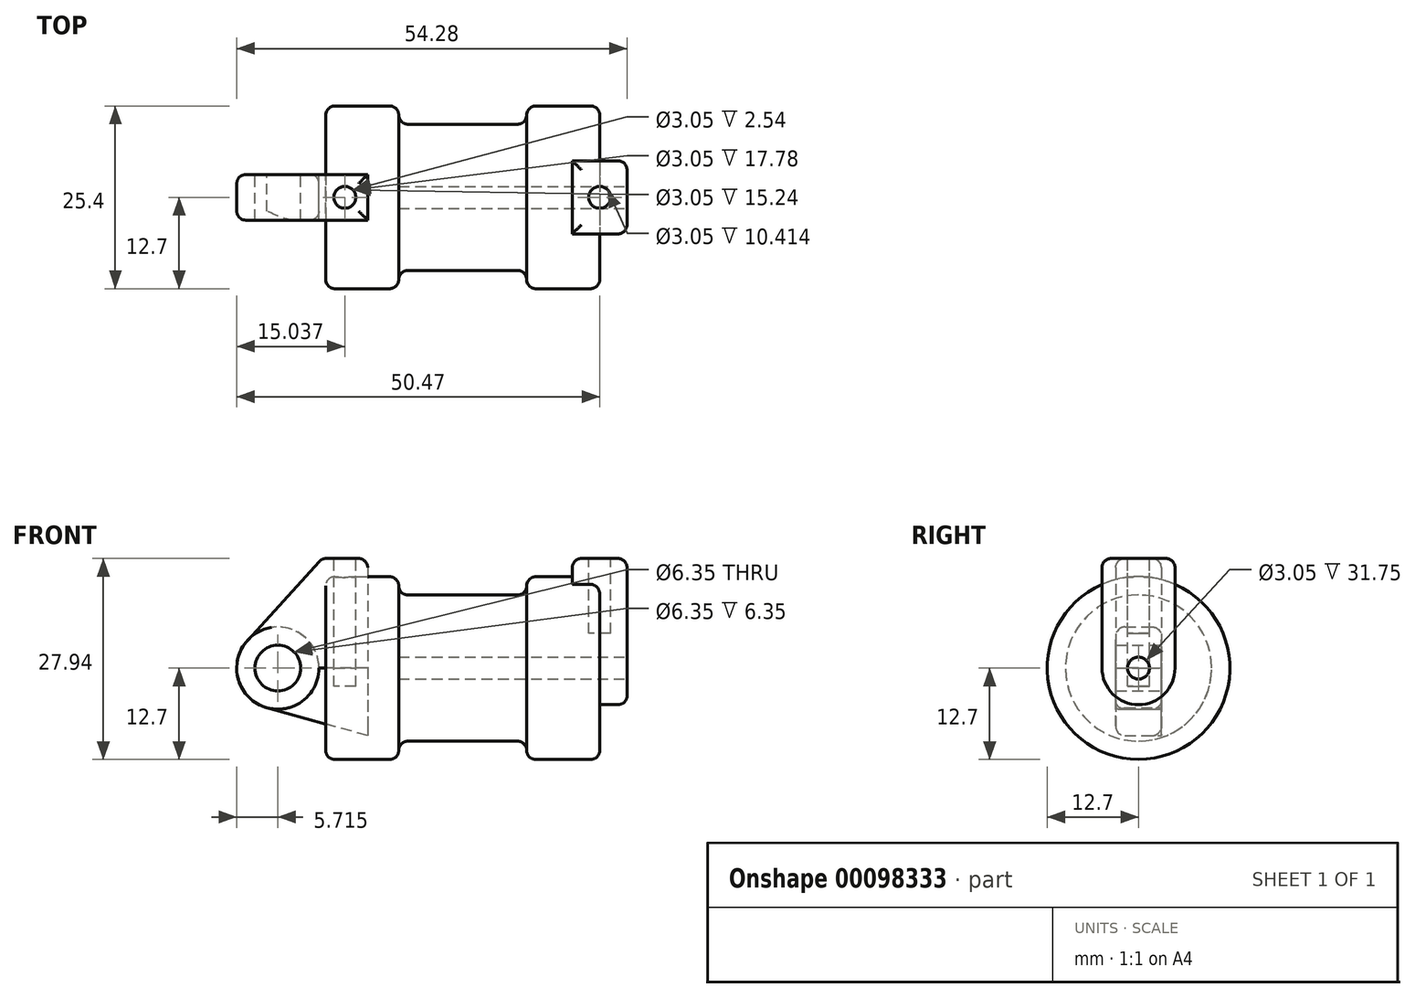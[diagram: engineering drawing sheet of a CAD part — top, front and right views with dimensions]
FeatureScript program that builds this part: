
annotation { "Feature Type Name" : "Feature", "Feature Type Description" : "" }
export const myFeature = defineFeature(function(context is Context, id is Id, definition is map)
    precondition{}
    {
        {
            var Q0;
            Q0=qCreatedBy(makeId("Front.planeOp"),FACE);
            var sketch = newSketch(context, id + "F0", { "sketchPlane" : qUnion([Q0])});
            skLineSegment(sketch, "E0", {"start": v(0, 0) * mm, "end": v(0, 12.7) * mm});
            skLineSegment(sketch, "E1", {"start": v(0, 12.7) * mm, "end": v(10.16, 12.7) * mm});
            skLineSegment(sketch, "E2", {"start": v(10.16, 12.7) * mm, "end": v(10.16, 10.16) * mm});
            skLineSegment(sketch, "E3", {"start": v(10.16, 10.16) * mm, "end": v(27.94, 10.16) * mm});
            skLineSegment(sketch, "E4", {"start": v(27.94, 10.16) * mm, "end": v(27.94, 12.7) * mm});
            skLineSegment(sketch, "E5", {"start": v(27.94, 12.7) * mm, "end": v(38.1, 12.7) * mm});
            skLineSegment(sketch, "E6", {"start": v(38.1, 12.7) * mm, "end": v(38.1, 0) * mm});
            skLineSegment(sketch, "E7", {"start": v(38.1, 0) * mm, "end": v(0, 0) * mm});
            skLineSegment(sketch, "E8", {"start": v(5.84, 15.24) * mm, "end": v(-0.5, 15.24) * mm});
            skLineSegment(sketch, "E9", {"start": v(-0.5, 15.24) * mm, "end": v(-10.88, 3.85) * mm});
            skLineSegment(sketch, "E10", {"start": v(0, 0) * mm, "end": v(-6.65, 0) * mm});
            skCircle(sketch, "E11", {"center": v(-6.65, 0) * mm, "radius": 5.72 * mm});
            skCircle(sketch, "E12", {"center": v(-6.65, 0) * mm, "radius": 3.18 * mm});
            skLineSegment(sketch, "E13", {"start": v(5.84, 15.24) * mm, "end": v(5.84, -9.4) * mm});
            skLineSegment(sketch, "E14", {"start": v(5.84, -9.4) * mm, "end": v(-8.18, -5.5) * mm});
            skSolve(sketch);
        }
        {
            var Q0;
            {var subQ0=sQuery(id+"F0.wireOp",EDGE,"E2");Q0=makeQuery(id+"F0.imprint","IMPRINT",FACE,{"disambiguationData":[TD([[makeQuery(id+"F0.imprint","IMPRINT",EDGE,{"derivedFrom":subQ0}),-1.0]])]});}
            var Q1;
            {var subQ0=sQuery(id+"F0.wireOp",EDGE,"E0");Q1=makeQuery(id+"F0.imprint","IMPRINT",FACE,{"disambiguationData":[TD([[makeQuery(id+"F0.imprint","IMPRINT",EDGE,{"derivedFrom":subQ0}),-1.0]])]});}
            var Q2;
            Q2=sQuery(id+"F0.wireOp",EDGE,"E7");
            revolve(context, id + "F1", {"entities" : qUnion([Q0, Q1]), "axis" : qUnion([Q2]), "revolveType" : RevolveType.FULL});
        }
        {
            var Q0;
            {var subQ4=sQuery(id+"F0.wireOp",EDGE,"E12");Q0=makeQuery(id+"F0.imprint","IMPRINT",FACE,{"disambiguationData":[TD([[makeQuery(id+"F0.imprint","IMPRINT",EDGE,{"derivedFrom":subQ4}),-1.0]])]});}
            extrude(context, id + "F2", {"entities" : qUnion([Q0]), "operationType" : NewBodyOperationType.ADD, "endBound" : BoundingType.SYMMETRIC, "depth" : 6.35 * mm});
        }
        {
            var Q0;
            {var subQ3=sQuery(id+"F0.wireOp",EDGE,"E0");Q0=makeQuery(id+"F0.imprint","IMPRINT",FACE,{"disambiguationData":[TD([[makeQuery(id+"F0.imprint","IMPRINT",EDGE,{"derivedFrom":subQ3}),1.0]])]});}
            var Q1;
            {var subQ0=sQuery(id+"F0.wireOp",EDGE,"E14");Q1=makeQuery(id+"F0.imprint","IMPRINT",FACE,{"disambiguationData":[TD([[makeQuery(id+"F0.imprint","IMPRINT",EDGE,{"derivedFrom":subQ0}),-1.0]])]});}
            var Q2;
            {var subQ4=sQuery(id+"F0.wireOp",EDGE,"E12");Q2=makeQuery(id+"F0.imprint","IMPRINT",FACE,{"disambiguationData":[TD([[makeQuery(id+"F0.imprint","IMPRINT",EDGE,{"derivedFrom":subQ4}),-1.0]])]});}
            var Q3;
            {var subQ0=sQuery(id+"F0.wireOp",EDGE,"E0");Q3=makeQuery(id+"F0.imprint","IMPRINT",FACE,{"disambiguationData":[TD([[makeQuery(id+"F0.imprint","IMPRINT",EDGE,{"derivedFrom":subQ0}),-1.0]])]});}
            extrude(context, id + "F3", {"entities" : qUnion([Q0, Q1, Q2, Q3]), "endBound" : BoundingType.SYMMETRIC, "depth" : 6.35 * mm});
        }
        {
            var Q0;
            {var subQ0=sQuery(id+"F0.wireOp",EDGE,"E14");Q0=makeQuery(id+"F0.imprint","IMPRINT",FACE,{"disambiguationData":[TD([[makeQuery(id+"F0.imprint","IMPRINT",EDGE,{"derivedFrom":subQ0}),-1.0]])]});}
            extrude(context, id + "F4", {"entities" : qUnion([Q0]), "endBound" : BoundingType.SYMMETRIC, "depth" : 6.35 * mm});
        }
        {
            var Q0;
            Q0=makeQuery(id+"F1.opRevolve","SWEPT_FACE",FACE,{"disambiguationData":[OSD([sQuery(id+"F0.wireOp",EDGE,"E6")])]});
            var sketch = newSketch(context, id + "F5", { "sketchPlane" : qUnion([Q0])});
            skCircle(sketch, "E15", {"center": v(0, 0) * mm, "radius": 1.52 * mm});
            skCircle(sketch, "E16", {"center": v(0, 0) * mm, "radius": 5.08 * mm});
            skLineSegment(sketch, "E17", {"start": v(-5.08, 0) * mm, "end": v(-5.08, 15.24) * mm});
            skLineSegment(sketch, "E18", {"start": v(5.08, 0) * mm, "end": v(5.08, 15.24) * mm});
            skLineSegment(sketch, "E19", {"start": v(-5.08, 15.24) * mm, "end": v(5.08, 15.24) * mm});
            skSolve(sketch);
        }
        {
            var Q0;
            {var subQ0=sQuery(id+"F5.wireOp",EDGE,"E19");Q0=makeQuery(id+"F5.imprint","IMPRINT",FACE,{"disambiguationData":[TD([[makeQuery(id+"F5.imprint","IMPRINT",EDGE,{"derivedFrom":subQ0}),-1.0]])]});}
            var Q1;
            {var subQ0=sQuery(id+"F5.wireOp",EDGE,"E17");var subQ1=sQuery(id+"F5.wireOp",EDGE,"E16");var subQ2=makeQuery(id+"F5.imprint","INTERSECT",VERTEX,{"derivedFrom":[subQ1,subQ0]});Q1=makeQuery(id+"F5.imprint","IMPRINT",FACE,{"disambiguationData":[TD([[makeQuery(id+"F5.imprint","IMPRINT",EDGE,{"disambiguationData":[TD([[subQ2,1.0]])],"derivedFrom":subQ1}),-1.0]])]});}
            var Q2;
            Q2=makeQuery(id+"F5.imprint","IMPRINT",FACE,{"disambiguationData":[TD([[makeQuery(id+"F5.imprint","IMPRINT",EDGE,{"derivedFrom":sQuery(id+"F5.wireOp",EDGE,"E15")}),-1.0]])]});
            extrude(context, id + "F6", {"entities" : qUnion([Q0, Q1, Q2]), "operationType" : NewBodyOperationType.ADD, "endBound" : BoundingType.SYMMETRIC, "oppositeDirection" : true, "depth" : 7.62 * mm});
        }
        {
            var Q0;
            Q0=makeQuery(id+"F5.imprint","IMPRINT",FACE,{"disambiguationData":[TD([[makeQuery(id+"F5.imprint","IMPRINT",EDGE,{"derivedFrom":sQuery(id+"F5.wireOp",EDGE,"E15")}),1.0]])]});
            var Q1;
            Q1=makeQuery(id+"F1.opRevolve","SWEPT_FACE",FACE,{"disambiguationData":[OSD([sQuery(id+"F0.wireOp",EDGE,"E2")])]});
            extrude(context, id + "F7", {"entities" : qUnion([Q0]), "operationType" : NewBodyOperationType.REMOVE, "endBound" : BoundingType.UP_TO_SURFACE, "oppositeDirection" : true, "endBoundEntityFace" : qUnion([Q1]), "depth" : 25.4 * mm});
        }
        {
            var Q0;
            Q0=makeQuery(id+"F3.opExtrude","SWEPT_FACE",FACE,{"disambiguationData":[OSD([sQuery(id+"F0.wireOp",EDGE,"E8")])]});
            var sketch = newSketch(context, id + "F8", { "sketchPlane" : qUnion([Q0])});
            skCircle(sketch, "E20", {"center": v(38.1, 0) * mm, "radius": 1.52 * mm});
            skPoint(sketch, "E21", {"position": v(2.67, 0) * mm});
            skCircle(sketch, "E22", {"center": v(2.67, 0) * mm, "radius": 1.52 * mm});
            skSolve(sketch);
        }
        {
            var Q0;
            Q0=makeQuery(id+"F8.imprint","IMPRINT",FACE,{"disambiguationData":[TD([[makeQuery(id+"F8.imprint","IMPRINT",EDGE,{"derivedFrom":sQuery(id+"F8.wireOp",EDGE,"E22")}),1.0]])]});
            var Q1;
            Q1=sQuery(id+"F8.wireOp",EDGE,"E22");
            extrude(context, id + "F9", {"entities" : qUnion([Q0]), "operationType" : NewBodyOperationType.REMOVE, "surfaceEntities" : qUnion([Q1]), "oppositeDirection" : true, "depth" : 17.78 * mm});
        }
        {
            var Q0;
            Q0=makeQuery(id+"F8.imprint","IMPRINT",FACE,{"disambiguationData":[TD([[makeQuery(id+"F8.imprint","IMPRINT",EDGE,{"derivedFrom":sQuery(id+"F8.wireOp",EDGE,"E20")}),1.0]])]});
            var Q1;
            Q1=sQuery(id+"F8.wireOp",EDGE,"E20");
            extrude(context, id + "F10", {"entities" : qUnion([Q0]), "operationType" : NewBodyOperationType.REMOVE, "surfaceEntities" : qUnion([Q1]), "oppositeDirection" : true, "depth" : 10.4 * mm});
        }
        {
            var Q0;
            Q0=makeQuery(id+"F1.opRevolve","SWEPT_EDGE",EDGE,{"disambiguationData":[OSD([sQuery(id+"F0.wireOp",EDGE,"E2"),sQuery(id+"F0.wireOp",EDGE,"E3")])]});
            var Q1;
            Q1=makeQuery(id+"F1.opRevolve","SWEPT_EDGE",EDGE,{"disambiguationData":[OSD([sQuery(id+"F0.wireOp",EDGE,"E1"),sQuery(id+"F0.wireOp",EDGE,"E2")])]});
            var Q2;
            Q2=makeQuery(id+"F1.opRevolve","SWEPT_EDGE",EDGE,{"disambiguationData":[OSD([sQuery(id+"F0.wireOp",EDGE,"E4"),sQuery(id+"F0.wireOp",EDGE,"E5")])]});
            var Q3;
            Q3=makeQuery(id+"F1.opRevolve","SWEPT_EDGE",EDGE,{"disambiguationData":[OSD([sQuery(id+"F0.wireOp",EDGE,"E3"),sQuery(id+"F0.wireOp",EDGE,"E4")])]});
            var Q4;
            Q4=makeQuery(id+"F1.opRevolve","SWEPT_EDGE",EDGE,{"disambiguationData":[OSD([sQuery(id+"F0.wireOp",EDGE,"E5"),sQuery(id+"F0.wireOp",EDGE,"E6")])]});
            var Q5;
            Q5=makeQuery(id+"F6.opExtrude","CAP_EDGE",EDGE,{"disambiguationData":[OSD([sQuery(id+"F5.wireOp",EDGE,"E19")])],"isStart":true});
            var Q6;
            Q6=makeQuery(id+"F6.opExtrude","SWEPT_EDGE",EDGE,{"disambiguationData":[OSD([sQuery(id+"F5.wireOp",EDGE,"E18"),sQuery(id+"F5.wireOp",EDGE,"E19")])]});
            var Q7;
            Q7=makeQuery(id+"F6.opExtrude","CAP_EDGE",EDGE,{"disambiguationData":[OSD([sQuery(id+"F5.wireOp",EDGE,"E19")])],"isStart":false});
            var Q8;
            Q8=makeQuery(id+"F6.opExtrude","SWEPT_EDGE",EDGE,{"disambiguationData":[OSD([sQuery(id+"F5.wireOp",EDGE,"E17"),sQuery(id+"F5.wireOp",EDGE,"E19")])]});
            var Q9;
            Q9=makeQuery(id+"F6.opExtrude","CAP_EDGE",EDGE,{"disambiguationData":[OSD([sQuery(id+"F5.wireOp",EDGE,"E16")])],"isStart":true});
            var Q10;
            Q10=makeQuery(id+"F6.opExtrude","CAP_EDGE",EDGE,{"disambiguationData":[OSD([sQuery(id+"F5.wireOp",EDGE,"E17")])],"isStart":true});
            var Q11;
            Q11=makeQuery(id+"F3.opExtrude","CAP_EDGE",EDGE,{"disambiguationData":[OSD([sQuery(id+"F0.wireOp",EDGE,"E8")])],"isStart":true});
            var Q12;
            Q12=makeQuery(id+"F3.opExtrude","SWEPT_EDGE",EDGE,{"disambiguationData":[OSD([sQuery(id+"F0.wireOp",EDGE,"E8"),sQuery(id+"F0.wireOp",EDGE,"E13")])]});
            var Q13;
            Q13=makeQuery(id+"F3.opExtrude","CAP_EDGE",EDGE,{"disambiguationData":[OSD([sQuery(id+"F0.wireOp",EDGE,"E8")])],"isStart":false});
            var Q14;
            Q14=makeQuery(id+"F3.opExtrude","SWEPT_EDGE",EDGE,{"disambiguationData":[OSD([sQuery(id+"F0.wireOp",EDGE,"E8"),sQuery(id+"F0.wireOp",EDGE,"E9")])]});
            var Q15;
            Q15=makeQuery(id+"F4.opExtrude","CAP_EDGE",EDGE,{"disambiguationData":[OSD([sQuery(id+"F0.wireOp",EDGE,"E14")])],"isStart":false});
            var Q16;
            Q16=makeQuery(id+"F3.opExtrude","CAP_EDGE",EDGE,{"disambiguationData":[OSD([sQuery(id+"F0.wireOp",EDGE,"E9")])],"isStart":true});
            var Q17;
            Q17=makeQuery(id+"F3.opExtrude","CAP_EDGE",EDGE,{"disambiguationData":[OSD([sQuery(id+"F0.wireOp",EDGE,"E9")])],"isStart":false});
            var Q18;
            Q18=makeQuery(id+"F2.opExtrude","SWEPT_FACE",FACE,{"disambiguationData":[OSD([sQuery(id+"F0.wireOp",EDGE,"E11")])]});
            var Q19;
            Q19=makeQuery(id+"F1.opRevolve","SWEPT_EDGE",EDGE,{"disambiguationData":[OSD([sQuery(id+"F0.wireOp",EDGE,"E0"),sQuery(id+"F0.wireOp",EDGE,"E1")])]});
            fillet(context, id + "F11", {"entities" : qUnion([Q0, Q1, Q2, Q3, Q4, Q5, Q6, Q7, Q8, Q9, Q10, Q11, Q12, Q13, Q14, Q15, Q16, Q17, Q18, Q19]), "radius" : 1.27 * mm, "tangentPropagation" : true, "allowEdgeOverflow" : false});
        }
    });
